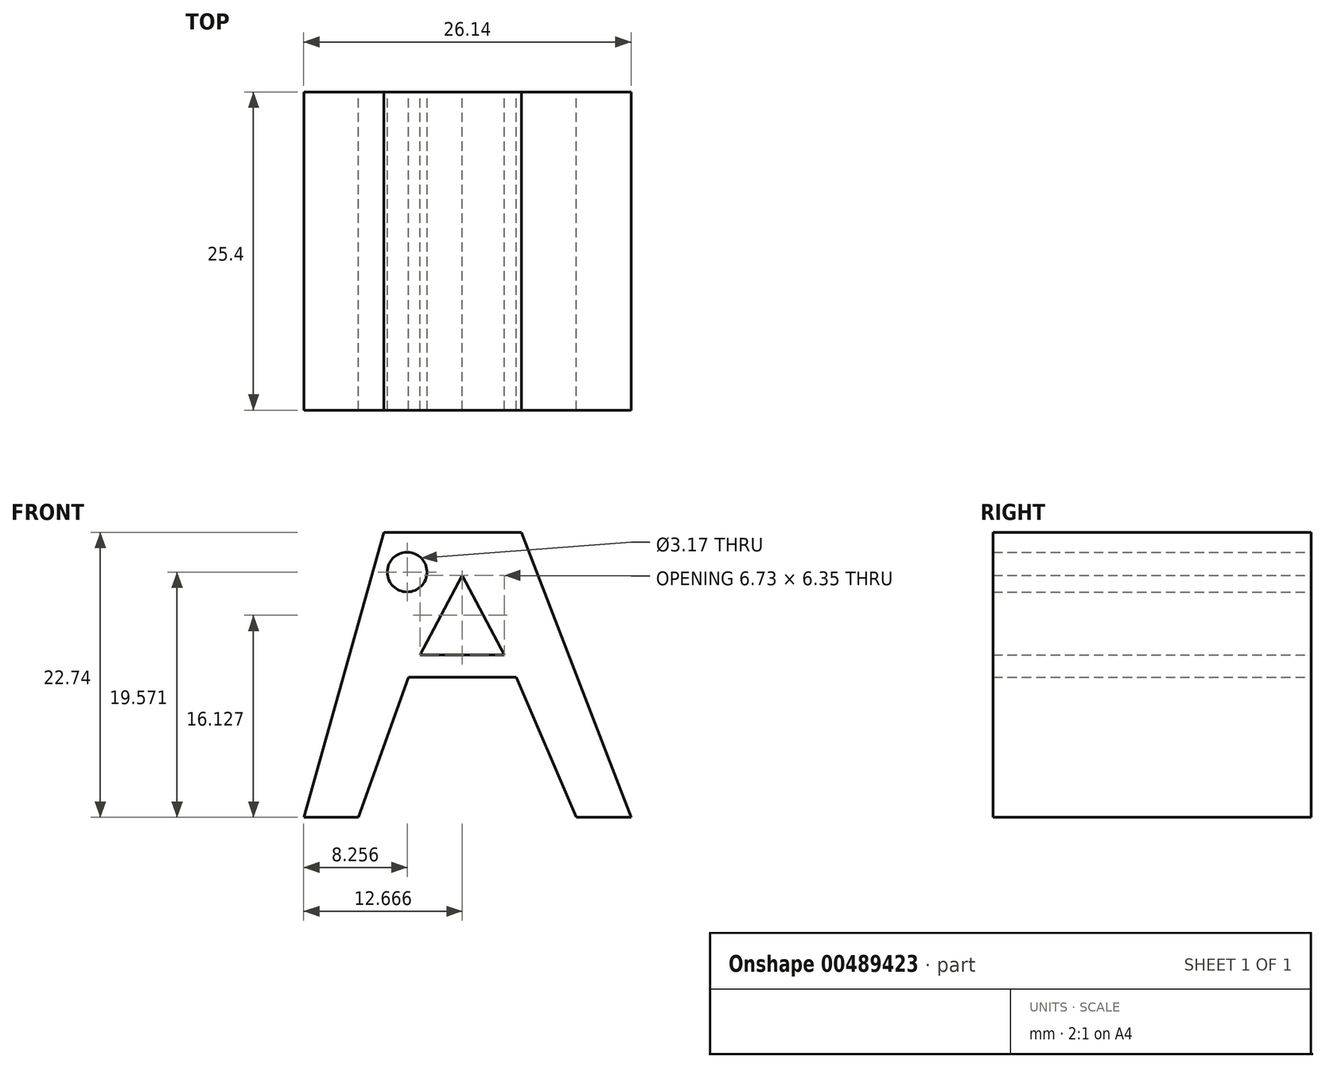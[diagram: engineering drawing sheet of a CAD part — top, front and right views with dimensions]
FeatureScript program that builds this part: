
annotation { "Feature Type Name" : "Feature", "Feature Type Description" : "" }
export const myFeature = defineFeature(function(context is Context, id is Id, definition is map)
    precondition{}
    {
        {
            var Q0;
            Q0=qCreatedBy(makeId("Front.planeOp"),FACE);
            var sketch = newSketch(context, id + "F0", { "sketchPlane" : qUnion([Q0])});
            skPoint(sketch, "E0.center.orphan", {"position": v(6.4, 36.28) * mm});
            skPoint(sketch, "E1.orphan", {"position": v(0, 35.54) * mm});
            skPoint(sketch, "E2.orphan", {"position": v(6.4, 35.54) * mm});
            skPoint(sketch, "E3.start.orphan", {"position": v(0, 23.17) * mm});
            skPoint(sketch, "E4.start.orphan", {"position": v(-2.74, 23.17) * mm});
            skPoint(sketch, "E5.orphan", {"position": v(-27.56, 23.17) * mm});
            skPoint(sketch, "E6.end.orphan", {"position": v(-2.74, 0) * mm});
            skLineSegment(sketch, "E7", {"start": v(-13.83, 22.74) * mm, "end": v(-5.1, 0) * mm});
            skLineSegment(sketch, "E8", {"start": v(-5.1, 0) * mm, "end": v(-9.46, 0) * mm});
            skLineSegment(sketch, "E9", {"start": v(-22.87, 11.19) * mm, "end": v(-26.87, 0) * mm});
            skPoint(sketch, "E10.orphan", {"position": v(-13.83, 0) * mm});
            skLineSegment(sketch, "E11", {"start": v(-22.87, 11.19) * mm, "end": v(-14.26, 11.19) * mm});
            skLineSegment(sketch, "E12", {"start": v(-14.26, 11.19) * mm, "end": v(-9.46, 0) * mm});
            skLineSegment(sketch, "E13", {"start": v(-22.87, 11.19) * mm, "end": v(-18.56, 19.3) * mm});
            skPoint(sketch, "E13.endSnap0", {"position": v(-18.56, 11.19) * mm});
            skLineSegment(sketch, "E14", {"start": v(-18.56, 19.3) * mm, "end": v(-14.26, 11.19) * mm});
            skLineSegment(sketch, "E15", {"start": v(-9.46, 0) * mm, "end": v(-5.1, 0) * mm});
            skPoint(sketch, "E16.start.orphan", {"position": v(-31.23, 0) * mm});
            skLineSegment(sketch, "E17", {"start": v(-26.87, 0) * mm, "end": v(-31.23, 0) * mm});
            skLineSegment(sketch, "E18", {"start": v(-31.23, 0) * mm, "end": v(-24.83, 22.74) * mm});
            skPoint(sketch, "E19.start.orphan", {"position": v(-22.87, 22.74) * mm});
            skLineSegment(sketch, "E20", {"start": v(-13.83, 22.74) * mm, "end": v(-24.83, 22.74) * mm});
            skLineSegment(sketch, "E21", {"start": v(-21.93, 12.95) * mm, "end": v(-15.2, 12.95) * mm});
            skCircle(sketch, "E22", {"center": v(-22.97, 19.57) * mm, "radius": 1.59 * mm});
            skSolve(sketch);
        }
        {
            var Q0;
            Q0 = qSketchRegion(id + "F0", true);
            extrude(context, id + "F1", {"entities" : qUnion([Q0]), "depth" : 25.4 * mm, "offsetDistance" : 25.4 * mm});
        }
        {
            var Q0;
            Q0 = qSketchRegion(id + "F0", true);
            var Q1;
            {var subQ3=sQuery(id+"F0.wireOp",EDGE,"E21");Q1=makeQuery(id+"F0.imprint","IMPRINT",FACE,{"disambiguationData":[TD([[makeQuery(id+"F0.imprint","IMPRINT",EDGE,{"derivedFrom":subQ3}),1.0]])]});}
            extrude(context, id + "F2", {"entities" : qUnion([Q0, Q1]), "operationType" : NewBodyOperationType.REMOVE, "oppositeDirection" : true, "depth" : 25.4 * mm, "offsetDistance" : 25.4 * mm});
        }
    });
